# Revit family: Electronics_Community-Point-Source_Biamp_Loudspeaker_IC6_2082WR
name_source: partatom
category: Communication Devices
units: mm (PartAtom-declared; Revit-internal decimal feet)

## family parameters
Cut with Voids When Loaded = No
Host = Face
Maintain Annotation Orientation = No
OmniClass Number = 23.85.10.11.14.14.14
OmniClass Title = Loudspeakers
Part Type = Normal
Room Calculation Point = No
Round Connector Dimension = Use Diameter
Shared = No

## types (12) — shared parameters
Default Elevation = 48 "
Depth = 10.62 "
Description = IC6-2082WR High Output Dual 8-Inch Two-Way Installation Loudspeaker
Environmental = Outdoor:  IP55W per IEC 60529, MIL-STD-810G
Equalized Maximum SPL = Peak - 130 dB; Continuosus - 124 dB
Equalized Sensitivity = 1W/1m - 99 dB; 2.83V - 96 dB
Height = 11.3 "
Input Connection = Screw terminal block (5-position)
Manufacturer = Biamp
Mounting Points = M10 threaded inserts; M8 threaded inserts (rear)
Operating Environment = Indoor or Weather-Resistant Outdoor
Operating Mode = Low Impedance or 70V/100V models
Product Documentation Link = https://downloads.biamp.com
Product Page URL = https://www.biamp.com
Product data url = https://www.bimobject.com
Recommended Amplifers = 300W -600W @ 16 ohms,  (69V - 98V)
Transducers = LF 2 x 8 (203mm) ferrite driver, 1.5 (37mm) voice coil, HF 1 x 1 (25mm) exit, 1.7 (44mm) voice coil, ketone polymer diaphragm, neodymium compression driver
URL = https://www.biamp.com
Width = 22.46 "

## per-type parameters (varying)
| type | Connector Description | Grill Material | Housing Material | Nominal Beamwidth  (H x V) | Nominal Maximum SPL | Nominal Sensitivity | Operating Range | Weight |
| IC6-2082WR26 G | Screw terminal block (5-position); Low impedance (16 ohm) | Biamp - Plastic - Gray(Grid) | Biamp - Plastic - Gray | 120° x  60° | Peak - 130 dB; Continuosus - 124 dB | 1W/1m - 92 dB; 2.83V - 92 dB | 49 Hz to 20 kHz | 23.90 lbf |
| IC6-2082WR26 W | Screw terminal block (5-position); Low impedance (16 ohm) | Biamp - Plastic - White(Grid) | Biamp - Plastic - White | 120° x  60° | Peak - 130 dB; Continuosus - 124 dB | 1W/1m - 92 dB; 2.83V - 92 dB | 49 Hz to 20 kHz | 23.90 lbf |
| IC6-2082WR26 B | Screw terminal block (5-position); Low impedance (16 ohm) | Biamp - Plastic - Black(Grid) | Biamp - Plastic - Black | 120° x  60° | Peak - 130 dB; Continuosus - 124 dB | 1W/1m - 92 dB; 2.83V - 92 dB | 49 Hz to 20 kHz | 23.90 lbf |
| IC6-2082WR96 G | Screw terminal block (5-position); Low impedance (16 ohm) | Biamp - Plastic - Gray(Grid) | Biamp - Plastic - Gray | 90° x  60° | Peak - 131 dB; Continuosus - 125 dB | 1W/1m - 100 dB; 2.83V - 97 dB | 50 Hz to 19.5 kHz | 23.90 lbf |
| IC6-2082WR96 W | Screw terminal block (5-position); Low impedance (16 ohm) | Biamp - Plastic - White(Grid) | Biamp - Plastic - White | 90° x  60° | Peak - 131 dB; Continuosus - 125 dB | 1W/1m - 100 dB; 2.83V - 97 dB | 50 Hz to 19.5 kHz | 23.90 lbf |
| IC6-2082WR96 B | Screw terminal block (5-position); Low impedance (16 ohm) | Biamp - Plastic - Black(Grid) | Biamp - Plastic - Black | 90° x  60° | Peak - 131 dB; Continuosus - 125 dB | 1W/1m - 100 dB; 2.83V - 97 dB | 50 Hz to 19.5 kHz | 23.90 lbf |
| IC6-2082WT26 G | Screw terminal block (5-position); 70/100V applications | Biamp - Plastic - Gray(Grid) | Biamp - Plastic - Gray | 120° x  60° | Peak - 130 dB; Continuosus - 124 dB | 1W/1m - 92 dB; 2.83V - 92 dB | 49 Hz to 20 kHz | 27.90 lbf |
| IC6-2082WT26 W | Screw terminal block (5-position); 70/100V applications | Biamp - Plastic - White(Grid) | Biamp - Plastic - White | 120° x  60° | Peak - 130 dB; Continuosus - 124 dB | 1W/1m - 92 dB; 2.83V - 92 dB | 49 Hz to 20 kHz | 27.90 lbf |
| IC6-2082WT26 B | Screw terminal block (5-position); 70/100V applications | Biamp - Plastic - Black(Grid) | Biamp - Plastic - Black | 120° x  60° | Peak - 130 dB; Continuosus - 124 dB | 1W/1m - 92 dB; 2.83V - 92 dB | 49 Hz to 20 kHz | 27.90 lbf |
| IC6-2082WT96 G | Screw terminal block (5-position); 70/100V applications | Biamp - Plastic - Gray(Grid) | Biamp - Plastic - Gray | 90° x  60° | Peak - 131 dB; Continuosus - 125 dB | 1W/1m - 100 dB; 2.83V - 97 dB | 50 Hz to 19.5 kHz | 27.90 lbf |
| IC6-2082WT96 W | Screw terminal block (5-position); 70/100V applications | Biamp - Plastic - White(Grid) | Biamp - Plastic - White | 90° x  60° | Peak - 131 dB; Continuosus - 125 dB | 1W/1m - 100 dB; 2.83V - 97 dB | 50 Hz to 19.5 kHz | 27.90 lbf |
| IC6-2082WT96 B | Screw terminal block (5-position); 70/100V applications | Biamp - Plastic - Black(Grid) | Biamp - Plastic - Black | 90° x  60° | Peak - 131 dB; Continuosus - 125 dB | 1W/1m - 100 dB; 2.83V - 97 dB | 50 Hz to 19.5 kHz | 27.90 lbf |

note: column(s) folded — value = type name in every type: Model

## geometry (parser evidence)
native form markers: Sweep x2
no freeform markers — native parametric forms only
